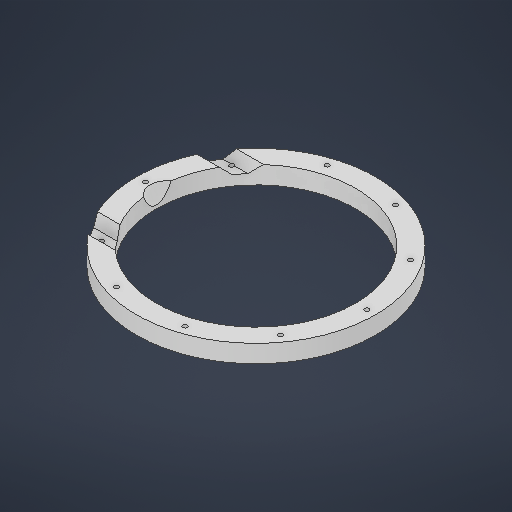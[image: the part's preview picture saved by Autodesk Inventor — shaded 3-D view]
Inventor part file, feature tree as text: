
AUTODESK INVENTOR PART (.ipt)
format: ipt  version: 2025 (Build 290162000, 162)  size: 244,736 bytes
history: native  units: in
note: dims shown in document units (in); Inventor stores cm internally (conversion verified against a paired STEP export)
features: sketch x5, extrude x3, plane x2, hole x1
ambient origin geometry x8: Origin, YZ Plane, XZ Plane, XY Plane, X Axis, Y Axis, Z Axis, Center Point
bodies: Solid1 (feature_tree)
feature tree (11):
  extrude  "Extrusion1"  Depth=8.8583in
  hole  "Hole1"  [1 undecoded]
  plane  "Work Plane6"
  plane  "Work Plane7"
  extrude  "Extrusion4"  Depth=3.937in TaperAngle=360.0deg
  extrude  "Extrusion5"  Depth=2.5in
  sketch  "Sketch1"  dims[d0=10.6299in d1=8.8583in]
  sketch  "Sketch3"  dims[d8=0.1969in d9=3.937in d11=360.0deg]
  sketch  "Sketch Circular Pattern1"  dims[d2=0.7874in d3=0.0in d7=9.8425in]
  sketch  "Sketch5"  dims[d13=0.1969in d14=0.2362in d15=0.1575in d16=0.0787in d17=90.0deg d18=0.315in d19=0.8108in d25=2.5in]
  sketch  "Sketch6"  dims[d26=1.5748in d27=3.3802in d28=9.8937in d29=0.0in d30=0.5512in d31=135.0deg d32=0.0in d33=0.0in d34=2.5591in d35=0.5512in d36=45.0deg]
note: 1 required parameter value undecoded (feature->parameter linkage not recoverable at this tier; creation-order binding heuristic only, values carry confidence <= 0.55)
